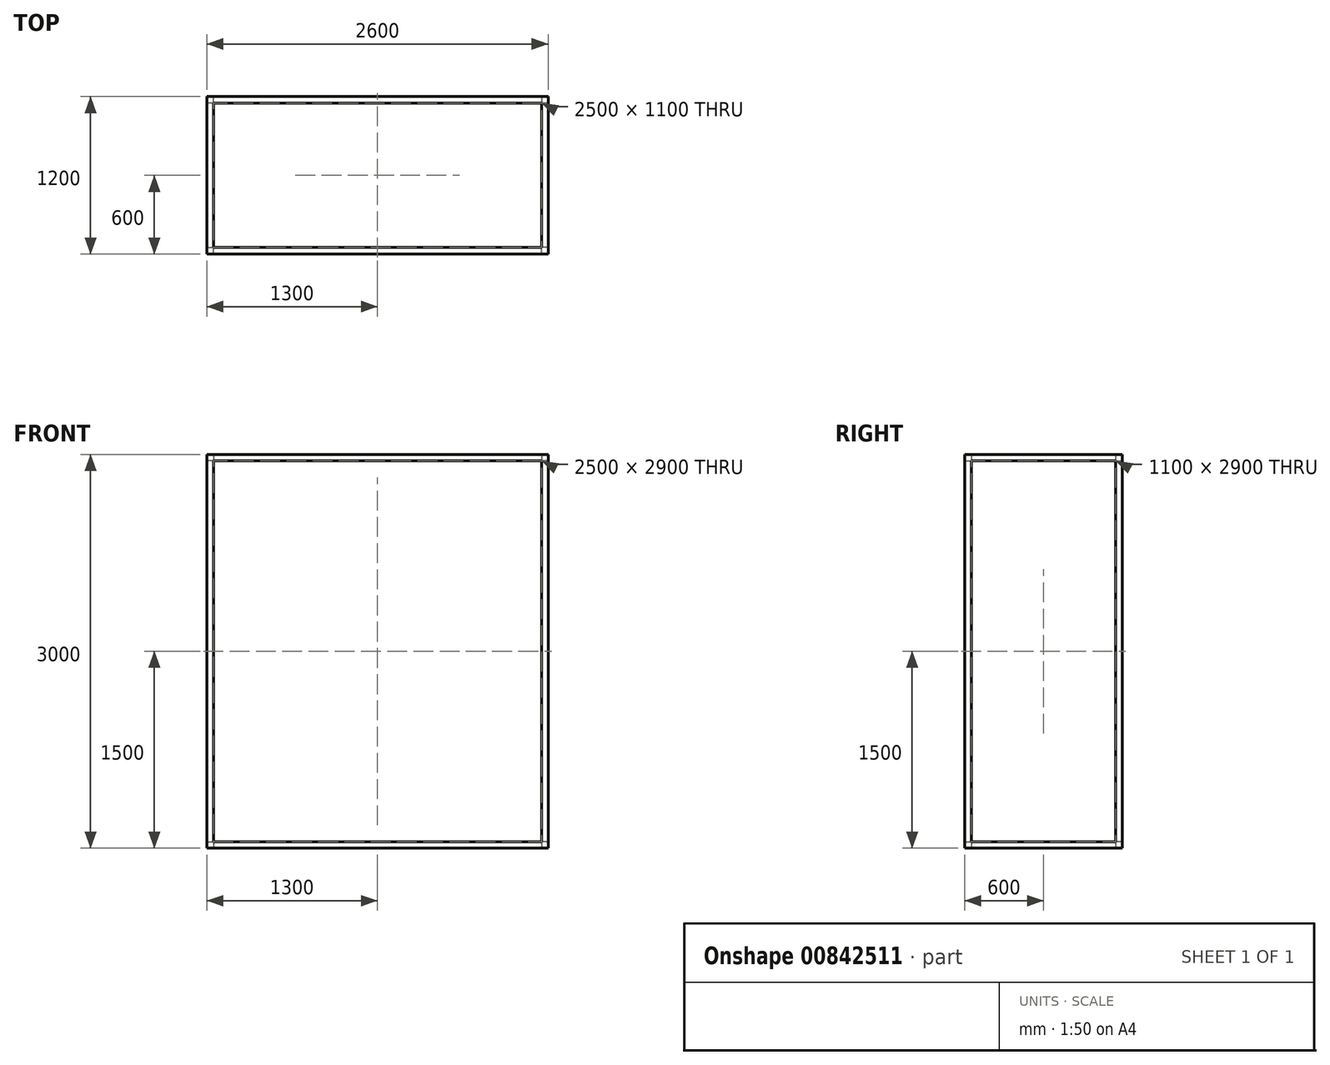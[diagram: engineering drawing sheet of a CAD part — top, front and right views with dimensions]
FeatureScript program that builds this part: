
annotation { "Feature Type Name" : "Feature", "Feature Type Description" : "" }
export const myFeature = defineFeature(function(context is Context, id is Id, definition is map)
    precondition{}
    {
        {
            var Q0;
            Q0=qCreatedBy(makeId("Top.planeOp"),FACE);
            var sketch = newSketch(context, id + "F0", { "sketchPlane" : qUnion([Q0])});
            skLineSegment(sketch, "E0.bottom", {"start": v(1300, 600) * mm, "end": v(-1300, 600) * mm});
            skLineSegment(sketch, "E0.top", {"start": v(1300, -600) * mm, "end": v(-1300, -600) * mm});
            skLineSegment(sketch, "E0.left", {"start": v(1300, 600) * mm, "end": v(1300, -600) * mm});
            skLineSegment(sketch, "E0.right", {"start": v(-1300, 600) * mm, "end": v(-1300, -600) * mm});
            skPoint(sketch, "E0.middle", {"position": v(0, 0) * mm});
            skLineSegment(sketch, "E1.bottom", {"start": v(1250, 550) * mm, "end": v(-1250, 550) * mm});
            skLineSegment(sketch, "E1.top", {"start": v(1250, -550) * mm, "end": v(-1250, -550) * mm});
            skLineSegment(sketch, "E1.left", {"start": v(1250, 550) * mm, "end": v(1250, -550) * mm});
            skLineSegment(sketch, "E1.right", {"start": v(-1250, 550) * mm, "end": v(-1250, -550) * mm});
            skSolve(sketch);
        }
        {
            var Q0;
            Q0 = qSketchRegion(id + "F0", true);
            extrude(context, id + "F1", {"entities" : qUnion([Q0]), "depth" : 50 * mm, "offsetDistance" : 25 * mm});
        }
        {
            var Q0;
            Q0=makeQuery(id+"F1.opExtrude","CAP_FACE",FACE,{"disambiguationData":[OSD([sQuery(id+"F0.wireOp",EDGE,"E0.bottom"),sQuery(id+"F0.wireOp",EDGE,"E0.top"),sQuery(id+"F0.wireOp",EDGE,"E0.left"),sQuery(id+"F0.wireOp",EDGE,"E0.right"),sQuery(id+"F0.wireOp",EDGE,"E1.bottom"),sQuery(id+"F0.wireOp",EDGE,"E1.top"),sQuery(id+"F0.wireOp",EDGE,"E1.left"),sQuery(id+"F0.wireOp",EDGE,"E1.right")])],"isStart":false});
            var sketch = newSketch(context, id + "F2", { "sketchPlane" : qUnion([Q0])});
            skLineSegment(sketch, "E2.bottom", {"start": v(-1250, 550) * mm, "end": v(-1300, 550) * mm});
            skLineSegment(sketch, "E2.top", {"start": v(-1250, 600) * mm, "end": v(-1300, 600) * mm});
            skLineSegment(sketch, "E2.left", {"start": v(-1250, 550) * mm, "end": v(-1250, 600) * mm});
            skLineSegment(sketch, "E2.right", {"start": v(-1300, 550) * mm, "end": v(-1300, 600) * mm});
            skLineSegment(sketch, "E3.bottom", {"start": v(1300, 600) * mm, "end": v(1250, 600) * mm});
            skLineSegment(sketch, "E3.top", {"start": v(1300, 550) * mm, "end": v(1250, 550) * mm});
            skLineSegment(sketch, "E3.left", {"start": v(1300, 600) * mm, "end": v(1300, 550) * mm});
            skLineSegment(sketch, "E3.right", {"start": v(1250, 600) * mm, "end": v(1250, 550) * mm});
            skLineSegment(sketch, "E4.bottom", {"start": v(1300, -600) * mm, "end": v(1250, -600) * mm});
            skLineSegment(sketch, "E4.top", {"start": v(1300, -550) * mm, "end": v(1250, -550) * mm});
            skLineSegment(sketch, "E4.left", {"start": v(1300, -600) * mm, "end": v(1300, -550) * mm});
            skLineSegment(sketch, "E4.right", {"start": v(1250, -600) * mm, "end": v(1250, -550) * mm});
            skLineSegment(sketch, "E5.bottom", {"start": v(-1300, -600) * mm, "end": v(-1250, -600) * mm});
            skLineSegment(sketch, "E5.top", {"start": v(-1300, -550) * mm, "end": v(-1250, -550) * mm});
            skLineSegment(sketch, "E5.left", {"start": v(-1300, -600) * mm, "end": v(-1300, -550) * mm});
            skLineSegment(sketch, "E5.right", {"start": v(-1250, -600) * mm, "end": v(-1250, -550) * mm});
            skSolve(sketch);
        }
        {
            var Q0;
            Q0 = qSketchRegion(id + "F2", true);
            extrude(context, id + "F3", {"entities" : qUnion([Q0]), "operationType" : NewBodyOperationType.ADD, "depth" : 2900 * mm, "offsetDistance" : 25 * mm});
        }
        {
            var Q0;
            Q0=makeQuery(id+"F3.opExtrude","CAP_FACE",FACE,{"disambiguationData":[OSD([sQuery(id+"F2.wireOp",EDGE,"E2.bottom"),sQuery(id+"F2.wireOp",EDGE,"E2.top"),sQuery(id+"F2.wireOp",EDGE,"E2.left"),sQuery(id+"F2.wireOp",EDGE,"E2.right")])],"isStart":false});
            var sketch = newSketch(context, id + "F4", { "sketchPlane" : qUnion([Q0])});
            skLineSegment(sketch, "E6.bottom", {"start": v(-1300, 600) * mm, "end": v(1300, 600) * mm});
            skLineSegment(sketch, "E6.top", {"start": v(-1300, -600) * mm, "end": v(1300, -600) * mm});
            skLineSegment(sketch, "E6.left", {"start": v(-1300, 600) * mm, "end": v(-1300, -600) * mm});
            skLineSegment(sketch, "E6.right", {"start": v(1300, 600) * mm, "end": v(1300, -600) * mm});
            skLineSegment(sketch, "E7.bottom", {"start": v(-1250, 550) * mm, "end": v(1250, 550) * mm});
            skLineSegment(sketch, "E7.top", {"start": v(-1250, -550) * mm, "end": v(1250, -550) * mm});
            skLineSegment(sketch, "E7.left", {"start": v(-1250, 550) * mm, "end": v(-1250, -550) * mm});
            skLineSegment(sketch, "E7.right", {"start": v(1250, 550) * mm, "end": v(1250, -550) * mm});
            skSolve(sketch);
        }
        {
            var Q0;
            Q0 = qSketchRegion(id + "F4", true);
            extrude(context, id + "F5", {"entities" : qUnion([Q0]), "operationType" : NewBodyOperationType.ADD, "depth" : 50 * mm, "offsetDistance" : 25 * mm});
        }
    });
